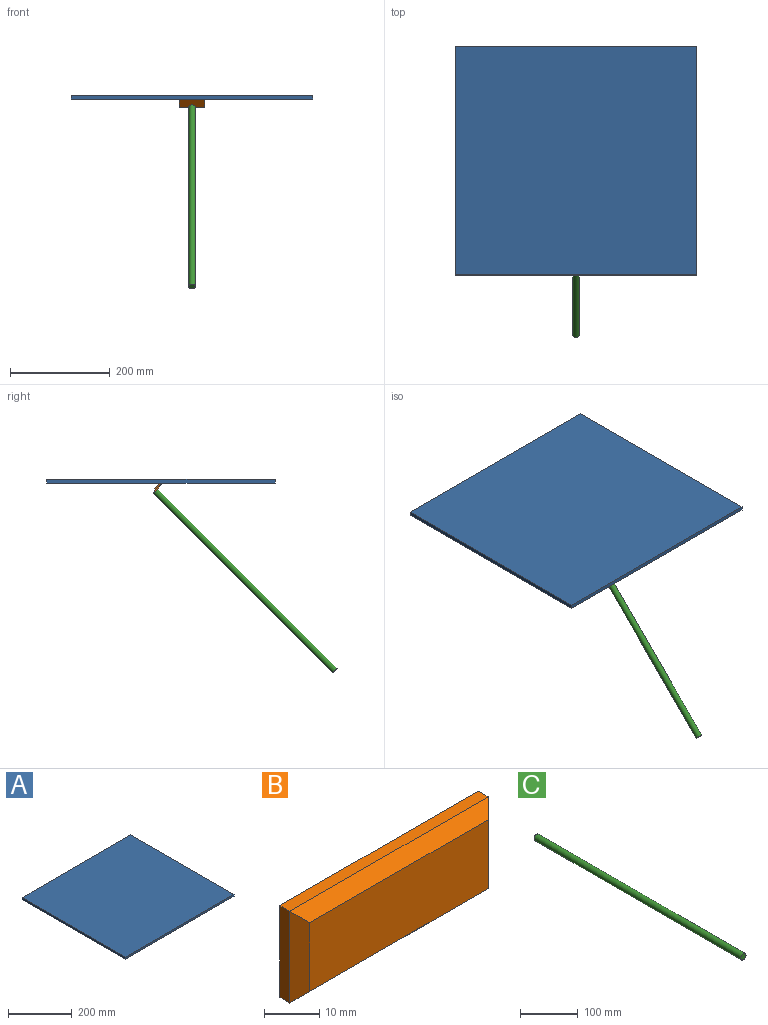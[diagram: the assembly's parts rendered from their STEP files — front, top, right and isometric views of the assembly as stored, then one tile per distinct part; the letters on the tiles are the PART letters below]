
ASSEMBLY  parts=3 mates=2
PART A: 6 faces, bbox 482.6x457.2x7.6 mm
  f0: plane 457.2x7.62mm, normal (1,0,0), area 3483.9mm2, adj f1,f3,f4,f5
  f1: plane 482.6x7.62mm, normal (0,1,0), area 3677.4mm2, adj f0,f2,f4,f5
  f2: plane 457.2x7.62mm, normal (-1,0,0), area 3483.9mm2, adj f1,f3,f4,f5
  f3: plane 482.6x7.62mm, normal (0,-1,0), area 3677.4mm2, adj f0,f2,f4,f5
  f4: plane 482.6x457.2mm, normal (0,0,1), area 220644.7mm2, adj f0,f1,f2,f3
  f5: plane 482.6x457.2mm, normal (0,0,-1), area 220644.7mm2, adj f0,f1,f2,f3
PART B: 10 faces, bbox 50.8x5.1x20.3 mm
  f0: plane 20.32x2.54mm, normal (1,0,0), area 51.6mm2, adj f1,f3,f5,f6
  f1: plane 50.8x2.54mm, normal (0,0,1), area 129mm2, adj f0,f2,f5,f7
  f2: plane 20.32x2.54mm, normal (-1,0,0), area 51.6mm2, adj f1,f3,f5,f9
  f3: plane 50.8x2.54mm, normal (0,0,-1), area 129mm2, adj f0,f2,f5,f8
  f4: plane 45.72x15.24mm, normal (0,-1,0), area 696.8mm2, adj f6,f7,f8,f9
  f5: plane 50.8x20.32mm, normal (0,1,0), area 1032.3mm2, adj f0,f1,f2,f3
  f6: plane 20.32x2.54mm, normal (0.71,-0.71,0), area 63.9mm2, adj f0,f4,f7,f8
  f7: plane 50.8x2.54mm, normal (0,-0.71,0.71), area 173.4mm2, adj f1,f4,f6,f9
  f8: plane 50.8x2.54mm, normal (0,-0.71,-0.71), area 173.4mm2, adj f3,f4,f6,f9
  f9: plane 20.32x2.54mm, normal (-0.71,-0.71,0), area 63.9mm2, adj f2,f4,f7,f8
PART C: 3 faces, bbox 12.7x508x12.7 mm
  f0: cylinder r=6.35mm len=508mm, axis (0,1,0), area 20268.3mm2, adj f1,f2
  f1: plane 12.7x12.7mm, normal (0,-1,0), area 126.7mm2, adj f0
  f2: plane 12.7x12.7mm, normal (0,1,0), area 126.7mm2, adj f0
PLACE A t=(4.25,-7.35,-3.68)mm
PLACE B rot(axis=(0,0.38,-0.92),180deg) t=(4.25,496.99,-39.22)mm
PLACE C rot(axis=(1,0,0),45deg) t=(4.25,477.62,-19.84)mm
MATE fastened C.f0 <-> B.f5  axis (0,0.71,0.71) through (4.25,477.62,-19.84)mm
MATE fastened B.f7 <-> A.f5  axis (0,0,1) through (4.25,466.81,-3.68)mm
